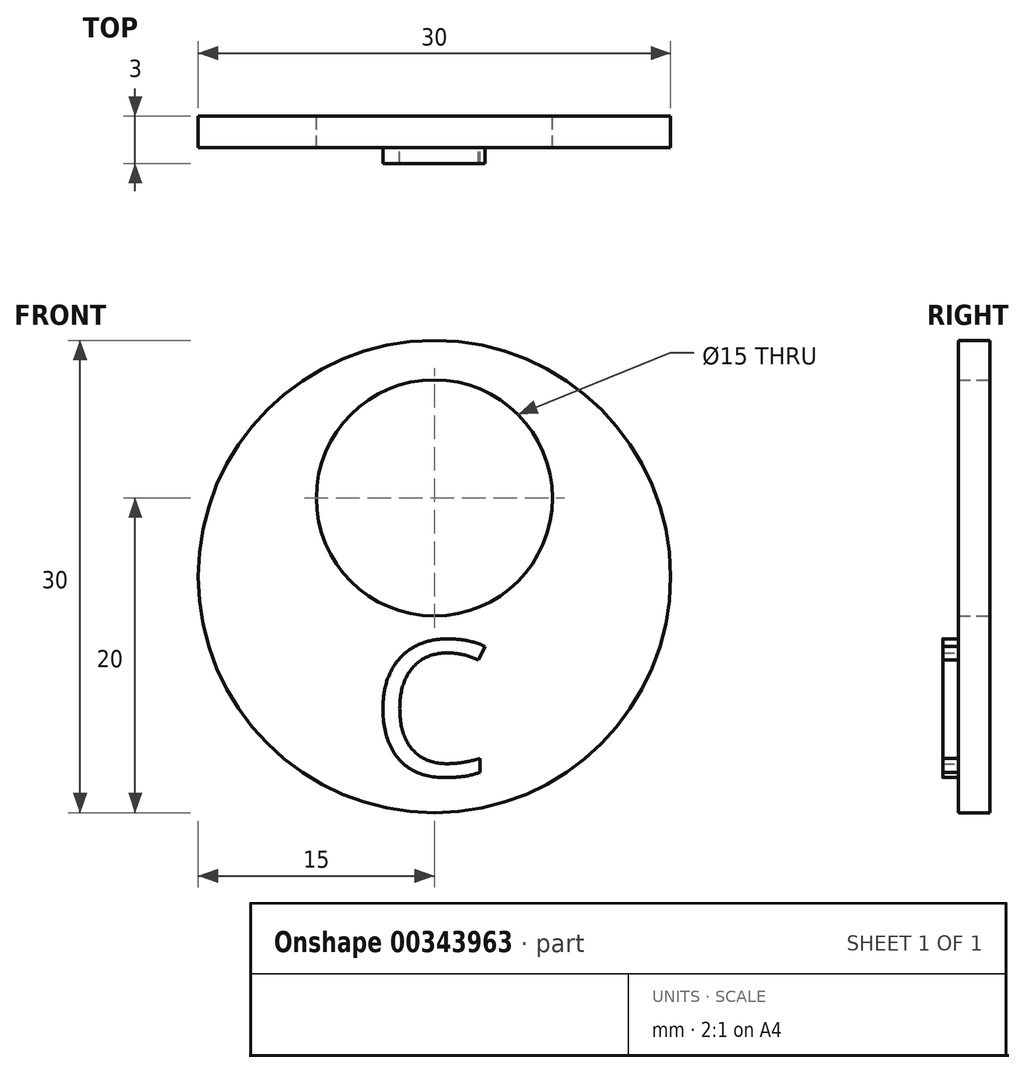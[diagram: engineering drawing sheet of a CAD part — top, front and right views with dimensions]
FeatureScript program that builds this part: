
annotation { "Feature Type Name" : "Feature", "Feature Type Description" : "" }
export const myFeature = defineFeature(function(context is Context, id is Id, definition is map)
    precondition{}
    {
        {
            var Q0;
            Q0=qCreatedBy(makeId("Front.planeOp"),FACE);
            var sketch = newSketch(context, id + "F0", { "sketchPlane" : qUnion([Q0])});
            skCircle(sketch, "E0", {"center": v(0, 0) * mm, "radius": 15 * mm});
            skPoint(sketch, "E1", {"position": v(0, 5) * mm});
            skCircle(sketch, "E2", {"center": v(0, 5) * mm, "radius": 7.5 * mm});
            skSolve(sketch);
        }
        {
            var Q0;
            Q0=makeQuery(id+"F0.imprint","IMPRINT",FACE,{"disambiguationData":[TD([[makeQuery(id+"F0.imprint","IMPRINT",EDGE,{"derivedFrom":sQuery(id+"F0.wireOp",EDGE,"E0")}),1.0]])]});
            extrude(context, id + "F1", {"entities" : qUnion([Q0]), "depth" : 2 * mm});
        }
        {
            var Q0;
            Q0=makeQuery(id+"F1.opExtrude","CAP_FACE",FACE,{"disambiguationData":[OSD([sQuery(id+"F0.wireOp",EDGE,"E0"),sQuery(id+"F0.wireOp",EDGE,"E2")])],"isStart":false});
            var sketch = newSketch(context, id + "F2", { "sketchPlane" : qUnion([Q0])});
            skText(sketch, "E3", { "text": "C", "fontName": "OpenSans-Regular.ttf"});
            const initialGuessF2  = {"E3": [-0.004, -0.01265, 1, 0, 0.00865]};
            skSetInitialGuess(sketch, initialGuessF2);
            skSolve(sketch);
        }
        {
            var Q0;
            Q0 = qSketchRegion(id + "F2", true);
            extrude(context, id + "F3", {"entities" : qUnion([Q0]), "operationType" : NewBodyOperationType.ADD, "depth" : 1 * mm});
        }
    });
